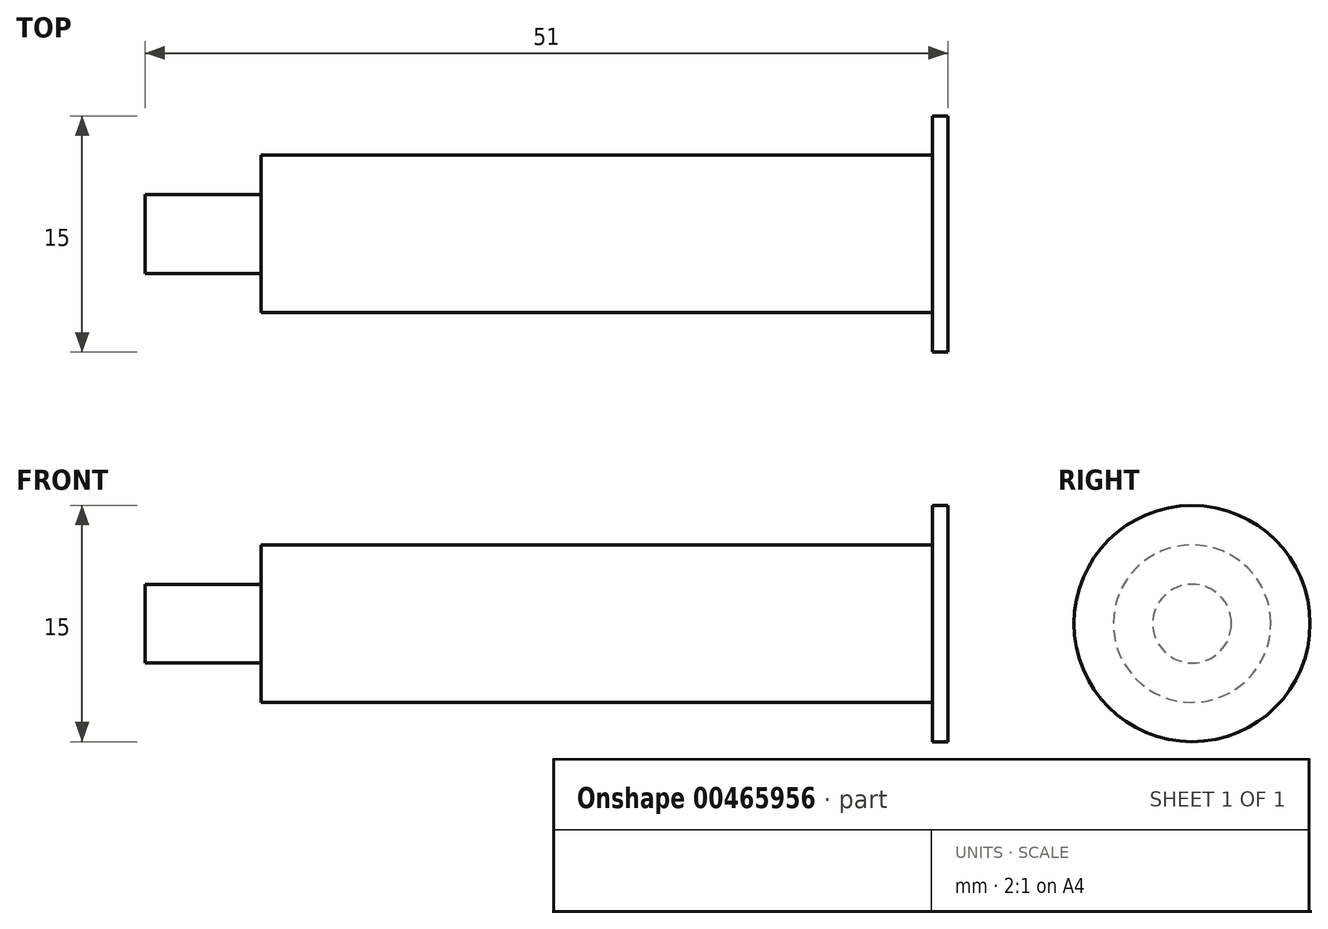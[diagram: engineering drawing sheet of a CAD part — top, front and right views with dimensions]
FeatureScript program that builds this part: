
annotation { "Feature Type Name" : "Feature", "Feature Type Description" : "" }
export const myFeature = defineFeature(function(context is Context, id is Id, definition is map)
    precondition{}
    {
        {
            var Q0;
            Q0=qCreatedBy(makeId("Front.planeOp"),FACE);
            var sketch = newSketch(context, id + "F0", { "sketchPlane" : qUnion([Q0])});
            skLineSegment(sketch, "E0", {"start": v(26, 5) * mm, "end": v(-16.63, 5) * mm});
            skLineSegment(sketch, "E1", {"start": v(-16.63, 5) * mm, "end": v(-16.63, 2.5) * mm});
            skLineSegment(sketch, "E2", {"start": v(-16.63, 2.5) * mm, "end": v(-24, 2.5) * mm});
            skLineSegment(sketch, "E3", {"start": v(-24, 2.5) * mm, "end": v(-24, 0) * mm});
            skLineSegment(sketch, "E4.top", {"start": v(26, 7.5) * mm, "end": v(27, 7.5) * mm});
            skLineSegment(sketch, "E4.right", {"start": v(27, 0) * mm, "end": v(27, 7.5) * mm});
            skLineSegment(sketch, "E5", {"start": v(26, 7.5) * mm, "end": v(26, 5) * mm});
            skLineSegment(sketch, "E6", {"start": v(-24, 0) * mm, "end": v(27, 0) * mm, "construction": true});
            skLineSegment(sketch, "E7", {"start": v(-24, 0) * mm, "end": v(27, 0) * mm});
            skSolve(sketch);
        }
        {
            var Q0;
            Q0=makeQuery(id+"F0.imprint","IMPRINT",FACE,{"disambiguationData":[TD([[makeQuery(id+"F0.imprint","IMPRINT",EDGE,{"derivedFrom":sQuery(id+"F0.wireOp",EDGE,"E0")}),1.0]])]});
            var Q1;
            Q1=sQuery(id+"F0.wireOp",EDGE,"E7");
            revolve(context, id + "F1", {"entities" : qUnion([Q0]), "axis" : qUnion([Q1]), "revolveType" : RevolveType.FULL});
        }
    });
